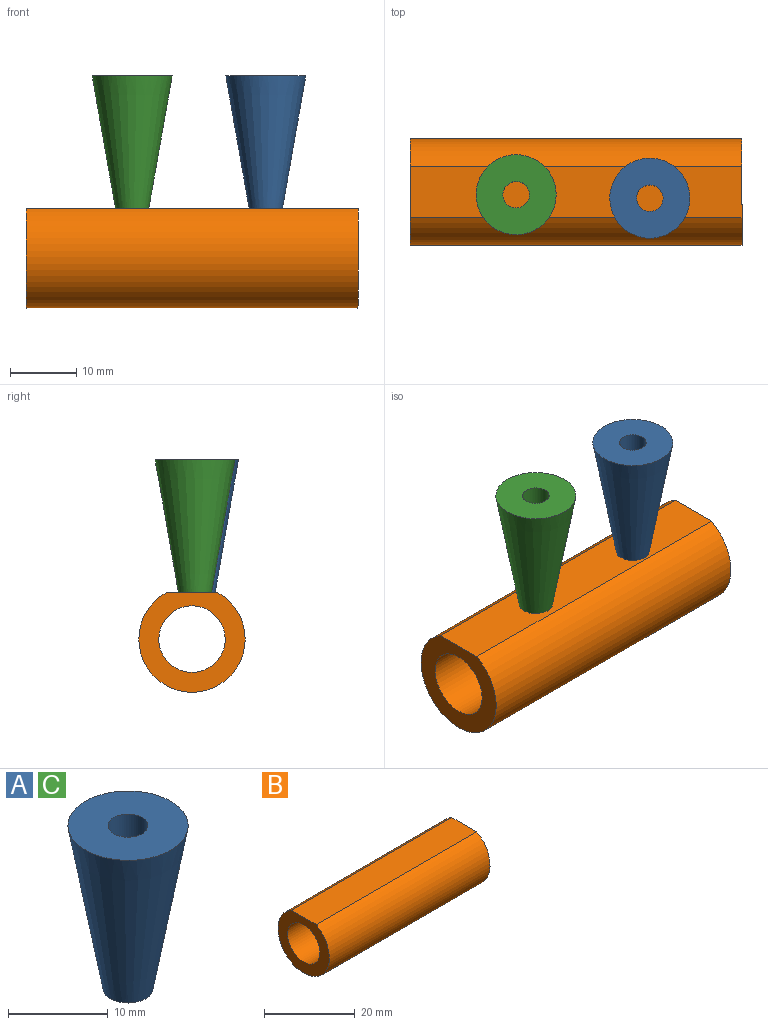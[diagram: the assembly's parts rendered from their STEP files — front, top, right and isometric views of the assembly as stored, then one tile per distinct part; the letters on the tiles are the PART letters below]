
ASSEMBLY  parts=3 mates=2
PART A: 4 faces, bbox 12.1x12.1x20 mm
  f0: cone r=2.5mm half-angle=10deg, axis (0,0,1), area 544mm2, adj f1,f2
  f1: plane 12.05x12.05mm, normal (0,0,1), area 101.5mm2, adj f0,f3
  f2: plane 5x5mm, normal (0,0,-1), area 7.1mm2, adj f0,f3
  f3: cylinder r=2mm len=20mm, axis (0,0,1), area 251.3mm2, adj f1,f2
PART B: 5 faces, bbox 50x16x15 mm
  f0: plane 16x15mm, normal (-1,0,0), area 117.3mm2, adj f1,f2,f4
  f1: cylinder r=5mm len=50mm, axis (-1,0,0), area 1570.8mm2, adj f0,f3
  f2: cylinder r=8mm len=50mm, axis (-1,0,0), area 2109mm2, adj f0,f3,f4
  f3: plane 16x15mm, normal (1,0,0), area 117.3mm2, adj f1,f2,f4
  f4: plane 50x7.75mm, normal (0,0,1), area 387.3mm2, adj f0,f2,f3
PART C: same geometry as A
PLACE A rot(axis=(0,0,-1),1.9deg) t=(11.22,-9.51,-1.62)mm
PLACE B t=(0.1,-8.52,-8.62)mm fixed
PLACE C rot(axis=(0,0,-1),0.6deg) t=(-8.91,-8.97,-1.62)mm
MATE planar C.f0 <-> B.f4  axis (0,0,-1) through (-8.91,-8.97,-1.62)mm
MATE parallel A.f0 <-> C.f3  axis (0,0,-1) through (11.22,-9.51,-1.62)mm
